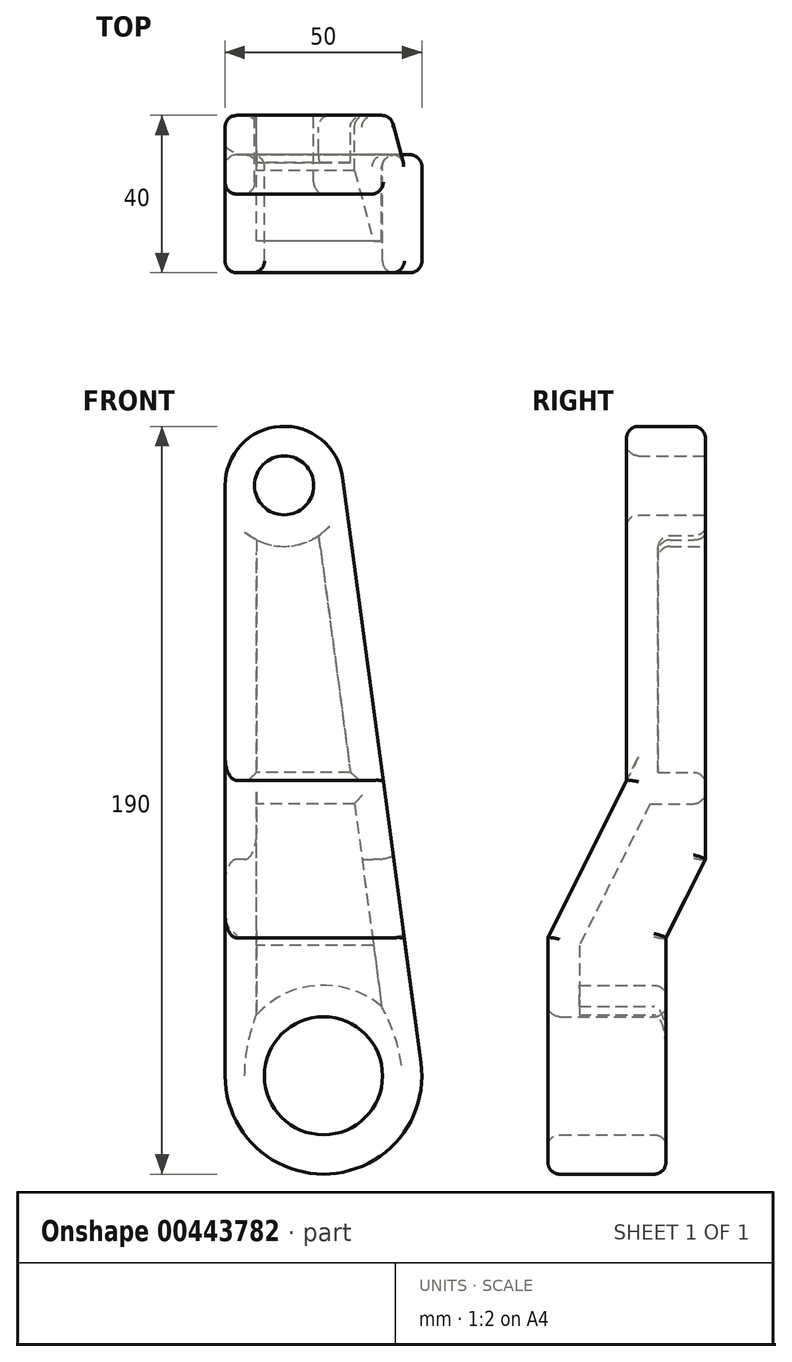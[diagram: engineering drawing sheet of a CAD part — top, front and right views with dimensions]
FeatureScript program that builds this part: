
annotation { "Feature Type Name" : "Feature", "Feature Type Description" : "" }
export const myFeature = defineFeature(function(context is Context, id is Id, definition is map)
    precondition{}
    {
        {
            var Q0;
            Q0=qCreatedBy(makeId("Front.planeOp"),FACE);
            var sketch = newSketch(context, id + "F0", { "sketchPlane" : qUnion([Q0])});
            skArc(sketch, "E0", {"start": v(-25, 0) * mm, "mid": v(1.66, -24.94) * mm, "end": v(24.78, 3.32) * mm});
            skArc(sketch, "E1", {"start": v(4.87, 152) * mm, "mid": v(-11, 164.97) * mm, "end": v(-25, 150) * mm});
            skLineSegment(sketch, "E2", {"start": v(4.87, 152) * mm, "end": v(24.78, 3.32) * mm});
            skLineSegment(sketch, "E3", {"start": v(-25, 150) * mm, "end": v(-25, 0) * mm});
            skSolve(sketch);
        }
        {
            var Q0;
            Q0 = qSketchRegion(id + "F0", true);
            extrude(context, id + "F1", {"entities" : qUnion([Q0]), "depth" : 40 * mm});
        }
        {
            var Q0;
            Q0=makeQuery(id+"F1.opExtrude","SWEPT_FACE",FACE,{"disambiguationData":[OSD([sQuery(id+"F0.wireOp",EDGE,"E3")])]});
            var sketch = newSketch(context, id + "F2", { "sketchPlane" : qUnion([Q0])});
            skLineSegment(sketch, "E4", {"start": v(0, 55) * mm, "end": v(0, -25.94) * mm});
            skLineSegment(sketch, "E5", {"start": v(10, -25.94) * mm, "end": v(10, 35) * mm});
            skLineSegment(sketch, "E6", {"start": v(40, 35) * mm, "end": v(20, 75) * mm});
            skLineSegment(sketch, "E7", {"start": v(20, 75) * mm, "end": v(20, 165.97) * mm});
            skLineSegment(sketch, "E8", {"start": v(40, 165.97) * mm, "end": v(40, 35) * mm});
            skLineSegment(sketch, "E9", {"start": v(10, 35) * mm, "end": v(0, 55) * mm});
            skLineSegment(sketch, "E10", {"start": v(0, -25.94) * mm, "end": v(10, -25.94) * mm});
            skLineSegment(sketch, "E11", {"start": v(40, 165.97) * mm, "end": v(20, 165.97) * mm});
            skSolve(sketch);
        }
        {
            var Q0;
            {var subQ0=sQuery(id+"F2.wireOp",EDGE,"E6");Q0=makeQuery(id+"F2.imprint","IMPRINT",FACE,{"disambiguationData":[TD([[makeQuery(id+"F2.imprint","IMPRINT",EDGE,{"derivedFrom":subQ0}),-1.0]])]});}
            var Q1;
            {var subQ0=sQuery(id+"F2.wireOp",EDGE,"JPgia858-IhdA-tNb5-Duaz-MfWCLMTx4JcA");Q1=makeQuery(id+"F2.imprint","IMPRINT",FACE,{"disambiguationData":[TD([[makeQuery(id+"F2.imprint","IMPRINT",EDGE,{"derivedFrom":subQ0}),-1.0]])]});}
            var Q2;
            {var subQ4=sQuery(id+"F2.wireOp",EDGE,"E9");Q2=makeQuery(id+"F2.imprint","IMPRINT",FACE,{"disambiguationData":[TD([[makeQuery(id+"F2.imprint","IMPRINT",EDGE,{"derivedFrom":subQ4}),1.0]])]});}
            var Q3;
            {var subQ3=sQuery(id+"F2.wireOp",EDGE,"qrfiZqFr-Lge9-3oEa-MpLj-D4ZgDNYpEj27");Q3=makeQuery(id+"F2.imprint","IMPRINT",FACE,{"disambiguationData":[TD([[makeQuery(id+"F2.imprint","IMPRINT",EDGE,{"derivedFrom":subQ3}),1.0]])]});}
            var Q4;
            {var subQ3=sQuery(id+"F2.wireOp",EDGE,"E10");Q4=makeQuery(id+"F2.imprint","IMPRINT",FACE,{"disambiguationData":[TD([[makeQuery(id+"F2.imprint","IMPRINT",EDGE,{"derivedFrom":subQ3}),1.0]])]});}
            var Q5;
            {var subQ0=sQuery(id+"F2.wireOp",EDGE,"E11");Q5=makeQuery(id+"F2.imprint","IMPRINT",FACE,{"disambiguationData":[TD([[makeQuery(id+"F2.imprint","IMPRINT",EDGE,{"derivedFrom":subQ0}),1.0]])]});}
            extrude(context, id + "F3", {"entities" : qUnion([Q0, Q1, Q2, Q3, Q4, Q5]), "operationType" : NewBodyOperationType.REMOVE, "endBound" : BoundingType.THROUGH_ALL, "oppositeDirection" : true, "depth" : 25 * mm});
        }
        {
            var Q0;
            Q0=makeQuery(id+"F1.opExtrude","CAP_FACE",FACE,{"disambiguationData":[OSD([sQuery(id+"F0.wireOp",EDGE,"E0"),sQuery(id+"F0.wireOp",EDGE,"E1"),sQuery(id+"F0.wireOp",EDGE,"E2"),sQuery(id+"F0.wireOp",EDGE,"E3")])],"isStart":true});
            var sketch = newSketch(context, id + "F4", { "sketchPlane" : qUnion([Q0])});
            skCircle(sketch, "E12", {"center": v(0, 0) * mm, "radius": 15 * mm});
            skCircle(sketch, "E13", {"center": v(10, 150) * mm, "radius": 7.5 * mm});
            skSolve(sketch);
        }
        {
            var Q0;
            Q0=makeQuery(id+"F4.imprint","IMPRINT",FACE,{"disambiguationData":[TD([[makeQuery(id+"F4.imprint","IMPRINT",EDGE,{"derivedFrom":sQuery(id+"F4.wireOp",EDGE,"E13")}),1.0]])]});
            var Q1;
            Q1=makeQuery(id+"F4.imprint","IMPRINT",FACE,{"disambiguationData":[TD([[makeQuery(id+"F4.imprint","IMPRINT",EDGE,{"derivedFrom":sQuery(id+"F4.wireOp",EDGE,"E12")}),1.0]])]});
            extrude(context, id + "F5", {"entities" : qUnion([Q0, Q1]), "operationType" : NewBodyOperationType.REMOVE, "endBound" : BoundingType.THROUGH_ALL, "oppositeDirection" : true, "depth" : 25 * mm});
        }
        {
            var Q0;
            Q0=makeQuery(id+"F1.opExtrude","CAP_FACE",FACE,{"disambiguationData":[OSD([sQuery(id+"F0.wireOp",EDGE,"E0"),sQuery(id+"F0.wireOp",EDGE,"E1"),sQuery(id+"F0.wireOp",EDGE,"E2"),sQuery(id+"F0.wireOp",EDGE,"E3")])],"isStart":true});
            var Q1;
            Q1=makeQuery(id+"F3.boolean.opBoolean","COPY",FACE,{"derivedFrom":makeQuery(id+"F3.opExtrude","SWEPT_FACE",FACE,{"disambiguationData":[OSD([sQuery(id+"F2.wireOp",EDGE,"E9")])]})});
            var Q2;
            Q2=makeQuery(id+"F3.boolean.opBoolean","COPY",FACE,{"derivedFrom":makeQuery(id+"F3.opExtrude","SWEPT_FACE",FACE,{"disambiguationData":[OSD([sQuery(id+"F2.wireOp",EDGE,"E5")])]})});
            shell(context, id + "F6", {"entities" : qUnion([Q0, Q1, Q2]), "thickness" : 8 * mm});
        }
        {
            var Q0;
            Q0=makeQuery(id+"F1.opExtrude","CAP_FACE",FACE,{"disambiguationData":[OSD([sQuery(id+"F0.wireOp",EDGE,"E0"),sQuery(id+"F0.wireOp",EDGE,"E1"),sQuery(id+"F0.wireOp",EDGE,"E2"),sQuery(id+"F0.wireOp",EDGE,"E3")])],"isStart":true});
            var sketch = newSketch(context, id + "F7", { "sketchPlane" : qUnion([Q0])});
            skLineSegment(sketch, "E14", {"start": v(-7.9, 69.11) * mm, "end": v(17, 69.11) * mm});
            skLineSegment(sketch, "E15", {"start": v(-6.82, 77.11) * mm, "end": v(17, 77.11) * mm});
            skLineSegment(sketch, "E16.0", {"start": v(-6.82, 77.11) * mm, "end": v(-7.9, 69.11) * mm});
            skLineSegment(sketch, "E17.0", {"start": v(17, 77.11) * mm, "end": v(17, 69.11) * mm});
            skPoint(sketch, "E18.orphan", {"position": v(1.23, 137.22) * mm});
            skPoint(sketch, "E19.orphan", {"position": v(-9.79, 55) * mm});
            skPoint(sketch, "E20.orphan", {"position": v(17, 55) * mm});
            skPoint(sketch, "E21.orphan", {"position": v(17, 136.17) * mm});
            skSolve(sketch);
        }
        {
            var Q0;
            Q0 = qSketchRegion(id + "F7", true);
            extrude(context, id + "F8", {"entities" : qUnion([Q0]), "operationType" : NewBodyOperationType.ADD, "endBound" : BoundingType.UP_TO_NEXT, "oppositeDirection" : true, "depth" : 25 * mm});
        }
        {
            var Q0;
            Q0=makeQuery(id+"F3.boolean.opBoolean","INTERSECT",EDGE,{"derivedFrom":[makeQuery(id+"F1.opExtrude","SWEPT_FACE",FACE,{"disambiguationData":[OSD([sQuery(id+"F0.wireOp",EDGE,"E2")])]}),makeQuery(id+"F3.opExtrude","SWEPT_FACE",FACE,{"disambiguationData":[OSD([sQuery(id+"F2.wireOp",EDGE,"E7")])]})]});
            var Q1;
            Q1=makeQuery(id+"F3.boolean.opBoolean","INTERSECT",EDGE,{"derivedFrom":[makeQuery(id+"F1.opExtrude","SWEPT_FACE",FACE,{"disambiguationData":[OSD([sQuery(id+"F0.wireOp",EDGE,"E2")])]}),makeQuery(id+"F3.opExtrude","SWEPT_FACE",FACE,{"disambiguationData":[OSD([sQuery(id+"F2.wireOp",EDGE,"E6")])]})]});
            var Q2;
            Q2=makeQuery(id+"F1.opExtrude","CAP_EDGE",EDGE,{"disambiguationData":[OSD([sQuery(id+"F0.wireOp",EDGE,"E2")])],"isStart":false});
            var Q3;
            Q3=makeQuery(id+"F1.opExtrude","CAP_EDGE",EDGE,{"disambiguationData":[OSD([sQuery(id+"F0.wireOp",EDGE,"E0")])],"isStart":false});
            var Q4;
            Q4=makeQuery(id+"F1.opExtrude","SWEPT_FACE",FACE,{"disambiguationData":[OSD([sQuery(id+"F0.wireOp",EDGE,"E1")])]});
            var Q5;
            Q5=makeQuery(id+"F3.boolean.opBoolean","INTERSECT",EDGE,{"derivedFrom":[makeQuery(id+"F1.opExtrude","SWEPT_FACE",FACE,{"disambiguationData":[OSD([sQuery(id+"F0.wireOp",EDGE,"E2")])]}),makeQuery(id+"F3.opExtrude","SWEPT_FACE",FACE,{"disambiguationData":[OSD([sQuery(id+"F2.wireOp",EDGE,"E5")])]})]});
            var Q6;
            Q6=makeQuery(id+"F3.boolean.opBoolean","INTERSECT",EDGE,{"derivedFrom":[makeQuery(id+"F1.opExtrude","SWEPT_FACE",FACE,{"disambiguationData":[OSD([sQuery(id+"F0.wireOp",EDGE,"E2")])]}),makeQuery(id+"F3.opExtrude","SWEPT_FACE",FACE,{"disambiguationData":[OSD([sQuery(id+"F2.wireOp",EDGE,"E9")])]})]});
            var Q7;
            Q7=makeQuery(id+"F1.opExtrude","CAP_EDGE",EDGE,{"disambiguationData":[OSD([sQuery(id+"F0.wireOp",EDGE,"E2")])],"isStart":true});
            var Q8;
            Q8=makeQuery(id+"F1.opExtrude","CAP_EDGE",EDGE,{"disambiguationData":[OSD([sQuery(id+"F0.wireOp",EDGE,"E3")])],"isStart":true});
            var Q9;
            Q9=makeQuery(id+"F3.boolean.opBoolean","COPY",EDGE,{"derivedFrom":makeQuery(id+"F3.opExtrude","CAP_EDGE",EDGE,{"disambiguationData":[OSD([sQuery(id+"F2.wireOp",EDGE,"E9")])],"isStart":true})});
            var Q10;
            Q10=makeQuery(id+"F3.boolean.opBoolean","COPY",EDGE,{"derivedFrom":makeQuery(id+"F3.opExtrude","CAP_EDGE",EDGE,{"disambiguationData":[OSD([sQuery(id+"F2.wireOp",EDGE,"E5")])],"isStart":true})});
            var Q11;
            Q11=makeQuery(id+"F3.boolean.opBoolean","INTERSECT",EDGE,{"derivedFrom":[makeQuery(id+"F1.opExtrude","SWEPT_FACE",FACE,{"disambiguationData":[OSD([sQuery(id+"F0.wireOp",EDGE,"E0")])]}),makeQuery(id+"F3.opExtrude","SWEPT_FACE",FACE,{"disambiguationData":[OSD([sQuery(id+"F2.wireOp",EDGE,"E5")])]})]});
            var Q12;
            Q12=makeQuery(id+"F3.boolean.opBoolean","COPY",EDGE,{"derivedFrom":makeQuery(id+"F3.opExtrude","CAP_EDGE",EDGE,{"disambiguationData":[OSD([sQuery(id+"F2.wireOp",EDGE,"E6")])],"isStart":true})});
            var Q13;
            Q13=makeQuery(id+"F3.boolean.opBoolean","COPY",EDGE,{"derivedFrom":makeQuery(id+"F3.opExtrude","SWEPT_EDGE",EDGE,{"disambiguationData":[OSD([sQuery(id+"F0.wireOp",EDGE,"E3"),sQuery(id+"F2.wireOp",EDGE,"E6"),sQuery(id+"F2.wireOp",EDGE,"E8")])]})});
            var Q14;
            Q14=makeQuery(id+"F1.opExtrude","CAP_EDGE",EDGE,{"disambiguationData":[OSD([sQuery(id+"F0.wireOp",EDGE,"E3")])],"isStart":false});
            var Q15;
            Q15=makeQuery(id+"F3.boolean.opBoolean","COPY",EDGE,{"derivedFrom":makeQuery(id+"F3.opExtrude","CAP_EDGE",EDGE,{"disambiguationData":[OSD([sQuery(id+"F2.wireOp",EDGE,"E7")])],"isStart":true})});
            var Q16;
            Q16=makeQuery(id+"F5.boolean.opBoolean","INTERSECT",EDGE,{"derivedFrom":[makeQuery(id+"F3.boolean.opBoolean","COPY",FACE,{"derivedFrom":makeQuery(id+"F3.opExtrude","SWEPT_FACE",FACE,{"disambiguationData":[OSD([sQuery(id+"F2.wireOp",EDGE,"E7")])]})}),makeQuery(id+"F5.opExtrude","SWEPT_FACE",FACE,{"disambiguationData":[OSD([sQuery(id+"F4.wireOp",EDGE,"E13")])]})]});
            var Q17;
            Q17=makeQuery(id+"F5.boolean.opBoolean","INTERSECT",EDGE,{"derivedFrom":[makeQuery(id+"F1.opExtrude","CAP_FACE",FACE,{"disambiguationData":[OSD([sQuery(id+"F0.wireOp",EDGE,"E0"),sQuery(id+"F0.wireOp",EDGE,"E1"),sQuery(id+"F0.wireOp",EDGE,"E2"),sQuery(id+"F0.wireOp",EDGE,"E3")])],"isStart":false}),makeQuery(id+"F5.opExtrude","SWEPT_FACE",FACE,{"disambiguationData":[OSD([sQuery(id+"F4.wireOp",EDGE,"E12")])]})]});
            var Q18;
            Q18=makeQuery(id+"F5.boolean.opBoolean","INTERSECT",EDGE,{"derivedFrom":[makeQuery(id+"F3.boolean.opBoolean","COPY",FACE,{"derivedFrom":makeQuery(id+"F3.opExtrude","SWEPT_FACE",FACE,{"disambiguationData":[OSD([sQuery(id+"F2.wireOp",EDGE,"E5")])]})}),makeQuery(id+"F5.opExtrude","SWEPT_FACE",FACE,{"disambiguationData":[OSD([sQuery(id+"F4.wireOp",EDGE,"E12")])]})]});
            var Q19;
            Q19=makeQuery(id+"F5.boolean.opBoolean","COPY",EDGE,{"derivedFrom":makeQuery(id+"F5.opExtrude","CAP_EDGE",EDGE,{"disambiguationData":[OSD([sQuery(id+"F4.wireOp",EDGE,"E13")])],"isStart":true})});
            var Q20;
            {var subQ1=sQuery(id+"F0.wireOp",EDGE,"E3");Q20=makeQuery(id+"F8.boolean.opBoolean","SPLIT",EDGE,{"disambiguationData":[TD([makeQuery(id+"F6.opShell","OFFSET_FACE",FACE,{"disambiguationData":[OSD([sQuery(id+"F4.wireOp",EDGE,"E13")])]})])],"derivedFrom":makeQuery(id+"F6.opShell","OFFSET_EDGE",EDGE,{"disambiguationData":[OSD([subQ1]),TDD([makeQuery(id+"F1.opExtrude","CAP_EDGE",EDGE,{"disambiguationData":[OSD([subQ1])],"isStart":true})])]})});}
            var Q21;
            Q21=makeQuery(id+"F6.opShell","OFFSET_EDGE",EDGE,{"disambiguationData":[OSD([sQuery(id+"F4.wireOp",EDGE,"E13")])]});
            var Q22;
            {var subQ1=sQuery(id+"F0.wireOp",EDGE,"E2");Q22=makeQuery(id+"F8.boolean.opBoolean","SPLIT",EDGE,{"disambiguationData":[TD([makeQuery(id+"F6.opShell","OFFSET_FACE",FACE,{"disambiguationData":[OSD([sQuery(id+"F4.wireOp",EDGE,"E13")])]})])],"derivedFrom":makeQuery(id+"F6.opShell","OFFSET_EDGE",EDGE,{"disambiguationData":[OSD([subQ1]),TDD([makeQuery(id+"F1.opExtrude","CAP_EDGE",EDGE,{"disambiguationData":[OSD([subQ1])],"isStart":true})])]})});}
            var Q23;
            Q23=makeQuery(id+"F8.opExtrude","CAP_EDGE",EDGE,{"disambiguationData":[OSD([sQuery(id+"F7.wireOp",EDGE,"E15")])],"isStart":true});
            var Q24;
            Q24=makeQuery(id+"F8.opExtrude","CAP_EDGE",EDGE,{"disambiguationData":[OSD([sQuery(id+"F7.wireOp",EDGE,"E14")])],"isStart":true});
            var Q25;
            {var subQ0=sQuery(id+"F0.wireOp",EDGE,"E2");Q25=makeQuery(id+"F8.boolean.opBoolean","SPLIT",EDGE,{"disambiguationData":[TD([makeQuery(id+"F6.opShell","OFFSET_FACE",FACE,{"disambiguationData":[OSD([sQuery(id+"F2.wireOp",EDGE,"E9")])]})])],"derivedFrom":makeQuery(id+"F6.opShell","OFFSET_EDGE",EDGE,{"disambiguationData":[OSD([subQ0]),TDD([makeQuery(id+"F1.opExtrude","CAP_EDGE",EDGE,{"disambiguationData":[OSD([subQ0])],"isStart":true})])]})});}
            var Q26;
            Q26=makeQuery(id+"F6.opShell","OFFSET_EDGE",EDGE,{"disambiguationData":[OSD([sQuery(id+"F2.wireOp",EDGE,"E9")])]});
            var Q27;
            Q27=makeQuery(id+"F6.opShell","OFFSET_EDGE",EDGE,{"disambiguationData":[OSD([sQuery(id+"F0.wireOp",EDGE,"E2"),sQuery(id+"F2.wireOp",EDGE,"E9")])]});
            var Q28;
            Q28=makeQuery(id+"F6.opShell","OFFSET_EDGE",EDGE,{"disambiguationData":[OSD([sQuery(id+"F0.wireOp",EDGE,"E2"),sQuery(id+"F2.wireOp",EDGE,"E5")])]});
            var Q29;
            Q29=makeQuery(id+"F6.opShell","OFFSET_EDGE",EDGE,{"disambiguationData":[OSD([sQuery(id+"F2.wireOp",EDGE,"E5"),sQuery(id+"F4.wireOp",EDGE,"E12")])]});
            var Q30;
            Q30=makeQuery(id+"F6.opShell","OFFSET_EDGE",EDGE,{"disambiguationData":[OSD([sQuery(id+"F2.wireOp",EDGE,"E5")])]});
            fillet(context, id + "F9", {"entities" : qUnion([Q0, Q1, Q2, Q3, Q4, Q5, Q6, Q7, Q8, Q9, Q10, Q11, Q12, Q13, Q14, Q15, Q16, Q17, Q18, Q19, Q20, Q21, Q22, Q23, Q24, Q25, Q26, Q27, Q28, Q29, Q30]), "radius" : 3 * mm, "tangentPropagation" : true, "allowEdgeOverflow" : false});
        }
    });
